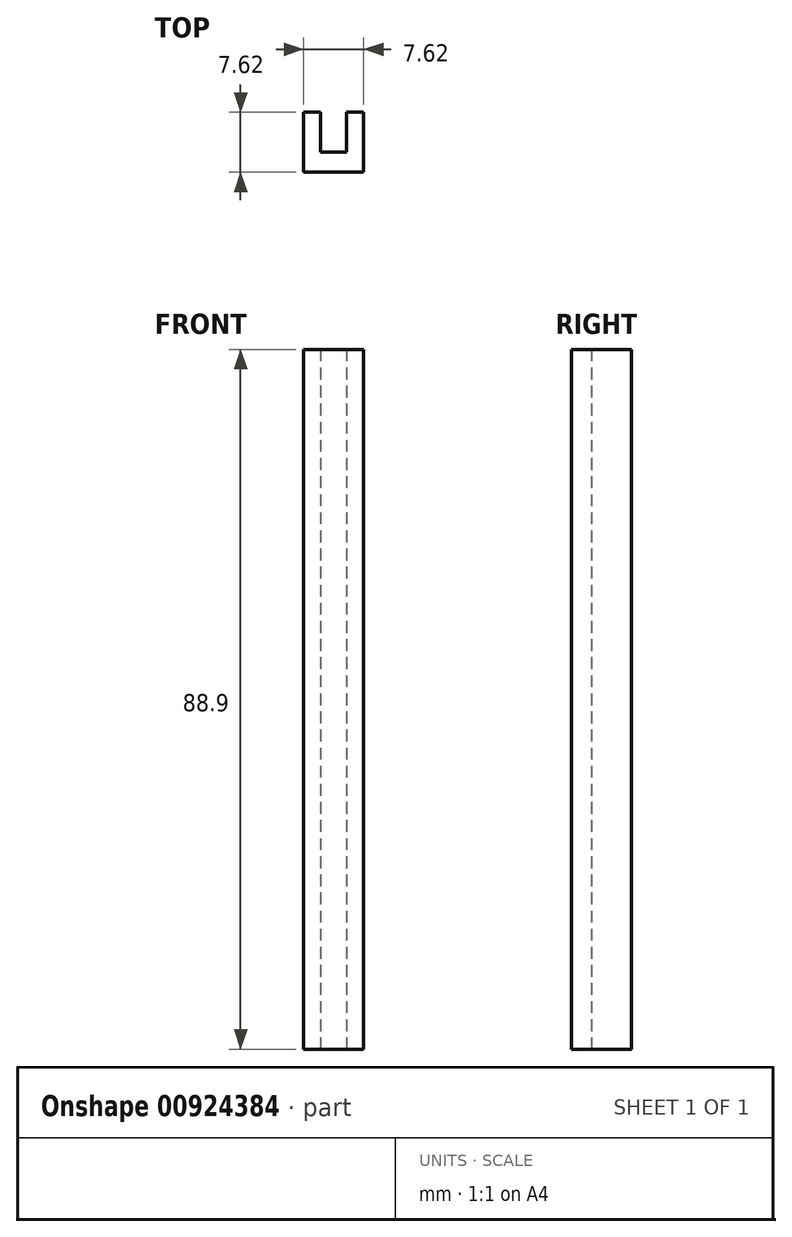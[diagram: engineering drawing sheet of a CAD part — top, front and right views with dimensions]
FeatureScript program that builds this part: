
annotation { "Feature Type Name" : "Feature", "Feature Type Description" : "" }
export const myFeature = defineFeature(function(context is Context, id is Id, definition is map)
    precondition{}
    {
        {
            var Q0;
            Q0=qCreatedBy(makeId("Top.planeOp"),FACE);
            var sketch = newSketch(context, id + "F0", { "sketchPlane" : qUnion([Q0])});
            skLineSegment(sketch, "E0.bottom", {"start": v(0, 0) * mm, "end": v(7.62, 0) * mm});
            skLineSegment(sketch, "E0.top", {"start": v(0, 7.62) * mm, "end": v(7.62, 7.62) * mm});
            skLineSegment(sketch, "E0.left", {"start": v(0, 0) * mm, "end": v(0, 7.62) * mm});
            skLineSegment(sketch, "E0.right", {"start": v(7.62, 0) * mm, "end": v(7.62, 7.62) * mm});
            skPoint(sketch, "E1", {"position": v(2.16, 7.62) * mm});
            skPoint(sketch, "E2", {"position": v(5.46, 7.62) * mm});
            skLineSegment(sketch, "E3.bottom", {"start": v(2.16, 7.62) * mm, "end": v(5.46, 7.62) * mm});
            skLineSegment(sketch, "E3.top", {"start": v(2.16, 2.54) * mm, "end": v(5.46, 2.54) * mm});
            skLineSegment(sketch, "E3.left", {"start": v(2.16, 7.62) * mm, "end": v(2.16, 2.54) * mm});
            skLineSegment(sketch, "E3.right", {"start": v(5.46, 7.62) * mm, "end": v(5.46, 2.54) * mm});
            skSolve(sketch);
        }
        {
            var Q0;
            Q0=makeQuery(id+"F0.imprint","IMPRINT",FACE,{"disambiguationData":[TD([[makeQuery(id+"F0.imprint","IMPRINT",EDGE,{"derivedFrom":sQuery(id+"F0.wireOp",EDGE,"E0.bottom")}),1.0]])]});
            extrude(context, id + "F1", {"entities" : qUnion([Q0]), "depth" : 88.9 * mm, "offsetDistance" : 25.4 * mm});
        }
    });
